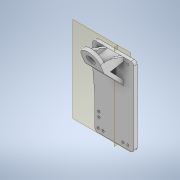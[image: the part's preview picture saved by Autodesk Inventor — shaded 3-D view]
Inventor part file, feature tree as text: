
AUTODESK INVENTOR PART (.ipt)
format: ipt  version: 2022 (Build 260153000, 153)  size: 488,960 bytes
history: native  units: mm
features: extrude x7, other x6, sketch x3, fillet x2, reference x1
ambient origin geometry x8: Origin, YZ Plane, XZ Plane, XY Plane, X Axis, Y Axis, Z Axis, Center Point
bodies: Body1 (feature_tree)
feature tree (19):
  other  "Твердое тело1"
  other  "РабПлоскость1"
  extrude  "Выдавливание1"  Depth=2.5mm TaperAngle=0.0deg
  other  "РабПлоскость3"
  sketch  "Эскиз7"
  extrude  "Выдавливание5"  Depth=6.0mm
  extrude  "Выдавливание6"  Depth=12.0mm
  fillet  "Сопряжение3"  Radius=7.0mm
  extrude  "Выдавливание7"  Depth=40.0mm
  extrude  "Выдавливание8"  Depth=14.0mm
  sketch  "Эскиз8"
  extrude  "Выдавливание9"  Depth=2.5mm
  extrude  "Выдавливание10"  Depth=2.5mm
  fillet  "Сопряжение4"  Radius=3.752458mm
  sketch  "Эскиз1"
  reference  "Ссылка1"
  other  "<userpath>\Documents\Inventor\AIM\Aim.iam"
  other  "Aim.iam"
  other  "Base:2"
